# Revit family: rba-bim-rba8851-137
name_source: partatom
category: Plumbing Fixtures
revit_build: Autodesk Revit 2016 (Build: 20151007_0715(x64)
units: mm (PartAtom-declared; Revit-internal decimal feet)

## family parameters
Cut with Voids When Loaded = Yes
Host = Face
OmniClass Number = 23.45.05.00
OmniClass Title = Sanitary Equipment
Part Type = Normal
Room Calculation Point = No
Round Connector Dimension = Use Diameter
Shared = Yes

## types (2) — shared parameters
CW Connection = Yes
Default Elevation = 426 mm
Description = Bariatric Toilet w/Optional Big John Toilet Seat
HW Connection = No
Manufacturer = RBA Group
Materials and Finishes = White Powder Coated SS
URL = http://www.rba.com.au
Vent Connection = No
Waste Connection = Yes

## per-type parameters (varying)
| type | Model | Modified Issue | P Trap | P Trap Connector | S Trap | S Trap Connector |
| rba8851-137 - P Trap | rba8851-137 |  | Yes | Yes | No | No |
| rba8851-137 - S Trap | RBA8851-137 | 20200109.01 | No | No | Yes | Yes |

## geometry (parser evidence)
native form markers: Blend x20, Sweep x5
no freeform markers — native parametric forms only
